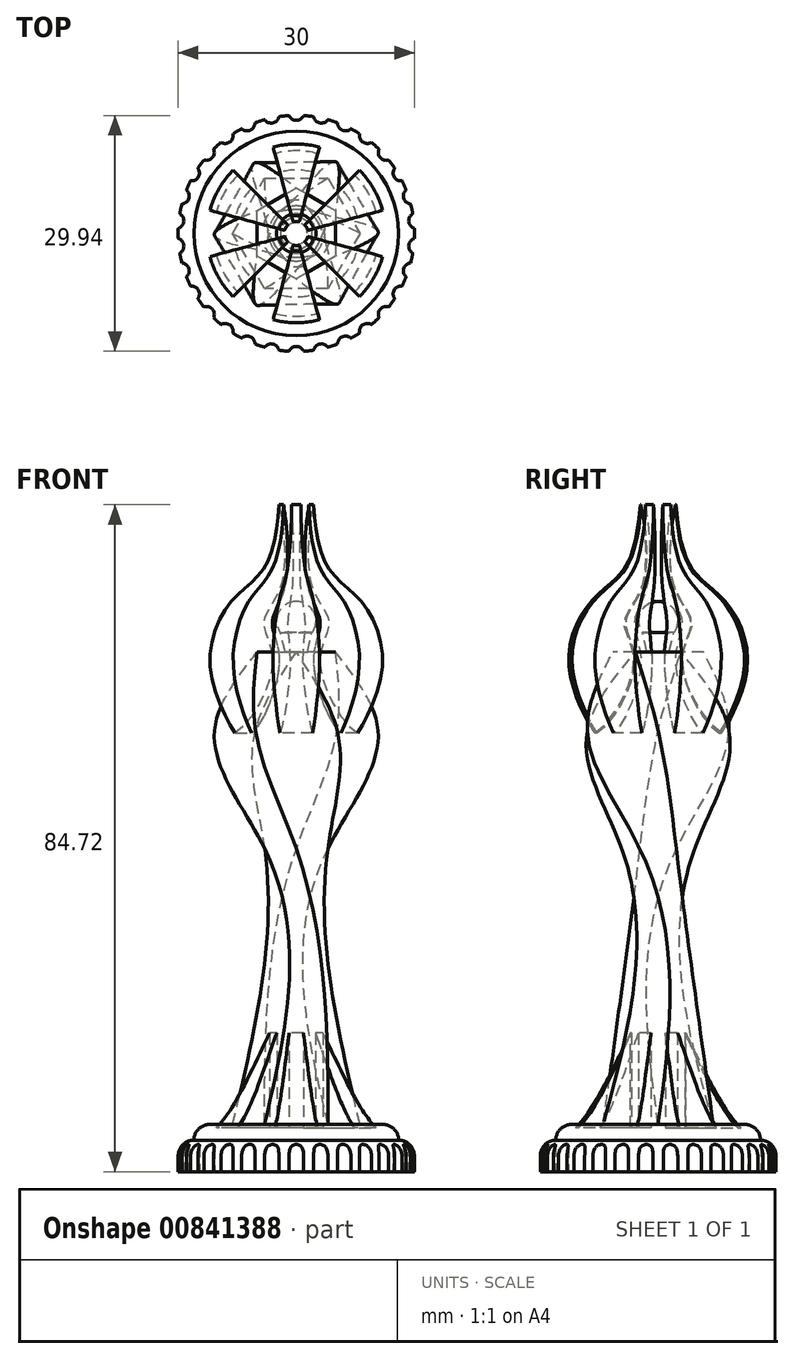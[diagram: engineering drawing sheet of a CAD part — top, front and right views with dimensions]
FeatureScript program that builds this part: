
annotation { "Feature Type Name" : "Feature", "Feature Type Description" : "" }
export const myFeature = defineFeature(function(context is Context, id is Id, definition is map)
    precondition{}
    {
        {
            var Q0;
            Q0=qCreatedBy(makeId("Top.planeOp"),FACE);
            var sketch = newSketch(context, id + "F0", { "sketchPlane" : qUnion([Q0])});
            skCircle(sketch, "E0", {"center": v(0, 0) * mm, "radius": 15 * mm});
            skSolve(sketch);
        }
        {
            var Q0;
            Q0=qSketchRegion(id+"F0",true);
            extrude(context, id + "F1", {"entities" : qUnion([Q0]), "depth" : 4 * mm, "offsetDistance" : 25 * mm});
        }
        {
            var Q0;
            Q0=makeQuery(id+"F1.opExtrude","CAP_FACE",FACE,{"disambiguationData":[OSD([sQuery(id+"F0.wireOp",EDGE,"E0")])],"isStart":false});
            var sketch = newSketch(context, id + "F2", { "sketchPlane" : qUnion([Q0])});
            skCircle(sketch, "E1", {"center": v(0, 0) * mm, "radius": 13 * mm});
            skSolve(sketch);
        }
        {
            var Q0;
            Q0=qSketchRegion(id+"F2",true);
            extrude(context, id + "F3", {"entities" : qUnion([Q0]), "operationType" : NewBodyOperationType.ADD, "depth" : 2 * mm, "offsetDistance" : 25 * mm});
        }
        {
            var Q0;
            Q0=makeQuery(id+"F1.opExtrude","CAP_EDGE",EDGE,{"disambiguationData":[OSD([sQuery(id+"F0.wireOp",EDGE,"E0")])],"isStart":false});
            var Q1;
            Q1=makeQuery(id+"F3.opExtrude","CAP_EDGE",EDGE,{"disambiguationData":[OSD([sQuery(id+"F2.wireOp",EDGE,"E1")])],"isStart":false});
            fillet(context, id + "F4", {"entities" : qUnion([Q0, Q1]), "radius" : 2 * mm, "tangentPropagation" : true, "allowEdgeOverflow" : false});
        }
        {
            var Q0;
            Q0=makeQuery(id+"F1.opExtrude","CAP_FACE",FACE,{"disambiguationData":[OSD([sQuery(id+"F0.wireOp",EDGE,"E0")])],"isStart":true});
            var sketch = newSketch(context, id + "F5", { "sketchPlane" : qUnion([Q0])});
            skCircle(sketch, "E2", {"center": v(0, 15.36) * mm, "radius": 1 * mm});
            skCircle(sketch, "E3.1.0", {"center": v(-3.2, 15.02) * mm, "radius": 1 * mm});
            skCircle(sketch, "E3.2.0", {"center": v(-6.25, 14.03) * mm, "radius": 1 * mm});
            skCircle(sketch, "E3.3.0", {"center": v(-9.03, 12.43) * mm, "radius": 1 * mm});
            skCircle(sketch, "E3.4.0", {"center": v(-11.41, 10.28) * mm, "radius": 1 * mm});
            skCircle(sketch, "E3.5.0", {"center": v(-13.3, 7.68) * mm, "radius": 1 * mm});
            skCircle(sketch, "E3.6.0", {"center": v(-14.6, 4.75) * mm, "radius": 1 * mm});
            skCircle(sketch, "E3.7.0", {"center": v(-15.27, 1.6) * mm, "radius": 1 * mm});
            skCircle(sketch, "E3.8.0", {"center": v(-15.27, -1.6) * mm, "radius": 1 * mm});
            skCircle(sketch, "E3.9.0", {"center": v(-14.6, -4.75) * mm, "radius": 1 * mm});
            skCircle(sketch, "E3.10.0", {"center": v(-13.3, -7.68) * mm, "radius": 1 * mm});
            skCircle(sketch, "E3.11.0", {"center": v(-11.41, -10.28) * mm, "radius": 1 * mm});
            skCircle(sketch, "E3.12.0", {"center": v(-9.03, -12.43) * mm, "radius": 1 * mm});
            skCircle(sketch, "E3.13.0", {"center": v(-6.25, -14.03) * mm, "radius": 1 * mm});
            skCircle(sketch, "E3.14.0", {"center": v(-3.2, -15.02) * mm, "radius": 1 * mm});
            skCircle(sketch, "E3.15.0", {"center": v(0, -15.36) * mm, "radius": 1 * mm});
            skCircle(sketch, "E3.16.0", {"center": v(3.2, -15.02) * mm, "radius": 1 * mm});
            skCircle(sketch, "E3.17.0", {"center": v(6.25, -14.03) * mm, "radius": 1 * mm});
            skCircle(sketch, "E3.18.0", {"center": v(9.03, -12.43) * mm, "radius": 1 * mm});
            skCircle(sketch, "E3.19.0", {"center": v(11.41, -10.28) * mm, "radius": 1 * mm});
            skCircle(sketch, "E3.20.0", {"center": v(13.3, -7.68) * mm, "radius": 1 * mm});
            skCircle(sketch, "E3.21.0", {"center": v(14.6, -4.75) * mm, "radius": 1 * mm});
            skCircle(sketch, "E3.22.0", {"center": v(15.27, -1.6) * mm, "radius": 1 * mm});
            skCircle(sketch, "E3.23.0", {"center": v(15.27, 1.6) * mm, "radius": 1 * mm});
            skCircle(sketch, "E3.24.0", {"center": v(14.6, 4.75) * mm, "radius": 1 * mm});
            skCircle(sketch, "E3.25.0", {"center": v(13.3, 7.68) * mm, "radius": 1 * mm});
            skCircle(sketch, "E3.26.0", {"center": v(11.41, 10.28) * mm, "radius": 1 * mm});
            skCircle(sketch, "E3.27.0", {"center": v(9.03, 12.43) * mm, "radius": 1 * mm});
            skCircle(sketch, "E3.28.0", {"center": v(6.25, 14.03) * mm, "radius": 1 * mm});
            skCircle(sketch, "E3.29.0", {"center": v(3.2, 15.02) * mm, "radius": 1 * mm});
            skPoint(sketch, "E3.center", {"position": v(0, 0) * mm});
            skSolve(sketch);
        }
        {
            var Q0;
            Q0=qSketchRegion(id+"F5",true);
            extrude(context, id + "F6", {"entities" : qUnion([Q0]), "operationType" : NewBodyOperationType.REMOVE, "oppositeDirection" : true, "depth" : 25 * mm, "offsetDistance" : 25 * mm});
        }
        {
            var Q0;
            Q0=makeQuery(id+"F3.opExtrude","CAP_FACE",FACE,{"disambiguationData":[OSD([sQuery(id+"F2.wireOp",EDGE,"E1")])],"isStart":false});
            var sketch = newSketch(context, id + "F7", { "sketchPlane" : qUnion([Q0])});
            skCircle(sketch, "E4.cCircle", {"center": v(0, 0) * mm, "radius": 7 * mm, "construction": true});
            skLineSegment(sketch, "E4.0", {"start": v(8.08, 0) * mm, "end": v(4.04, -7) * mm});
            skLineSegment(sketch, "E4.1", {"start": v(4.04, -7) * mm, "end": v(-4.04, -7) * mm});
            skLineSegment(sketch, "E4.2", {"start": v(-4.04, -7) * mm, "end": v(-8.08, 0) * mm});
            skLineSegment(sketch, "E4.3", {"start": v(-8.08, 0) * mm, "end": v(-4.04, 7) * mm});
            skLineSegment(sketch, "E4.4", {"start": v(-4.04, 7) * mm, "end": v(4.04, 7) * mm});
            skLineSegment(sketch, "E4.5", {"start": v(4.04, 7) * mm, "end": v(8.08, 0) * mm});
            skPoint(sketch, "E4.0.midPoint", {"position": v(6.06, -3.5) * mm});
            skSolve(sketch);
        }
        {
            var Q0;
            Q0=makeQuery(id+"F3.opExtrude","CAP_FACE",FACE,{"disambiguationData":[OSD([sQuery(id+"F2.wireOp",EDGE,"E1")])],"isStart":false});
            cPlane(context, id + "F8", {"entities" : qUnion([Q0]), "cplaneType" : CPlaneType.OFFSET, "offset" : 35 * mm, "width" : 150 * mm, "height" : 150 * mm});
        }
        {
            var Q0;
            Q0=qCreatedBy(id+"F8.planeOp",FACE);
            var sketch = newSketch(context, id + "F9", { "sketchPlane" : qUnion([Q0])});
            skCircle(sketch, "E5.cCircle", {"center": v(0, 0) * mm, "radius": 4 * mm, "construction": true});
            skLineSegment(sketch, "E5.0", {"start": v(4, 2.3) * mm, "end": v(4, -2.3) * mm});
            skLineSegment(sketch, "E5.1", {"start": v(4, -2.3) * mm, "end": v(0, -4.62) * mm});
            skLineSegment(sketch, "E5.2", {"start": v(0, -4.62) * mm, "end": v(-4, -2.3) * mm});
            skLineSegment(sketch, "E5.3", {"start": v(-4, -2.3) * mm, "end": v(-4, 2.3) * mm});
            skLineSegment(sketch, "E5.4", {"start": v(-4, 2.3) * mm, "end": v(0, 4.62) * mm});
            skLineSegment(sketch, "E5.5", {"start": v(0, 4.62) * mm, "end": v(4, 2.3) * mm});
            skPoint(sketch, "E5.0.midPoint", {"position": v(4, 0) * mm});
            skSolve(sketch);
        }
        {
            var Q0;
            Q0=qCreatedBy(id+"F8.planeOp",FACE);
            cPlane(context, id + "F10", {"entities" : qUnion([Q0]), "cplaneType" : CPlaneType.OFFSET, "offset" : 15 * mm, "width" : 150 * mm, "height" : 150 * mm});
        }
        {
            var Q0;
            Q0=qCreatedBy(id+"F10.planeOp",FACE);
            var sketch = newSketch(context, id + "F11", { "sketchPlane" : qUnion([Q0])});
            skCircle(sketch, "E6.cCircle", {"center": v(0, 0) * mm, "radius": 9 * mm, "construction": true});
            skLineSegment(sketch, "E6.0", {"start": v(5.2, -9) * mm, "end": v(-5.2, -9) * mm});
            skLineSegment(sketch, "E6.1", {"start": v(-5.2, -9) * mm, "end": v(-10.4, 0) * mm});
            skLineSegment(sketch, "E6.2", {"start": v(-10.4, 0) * mm, "end": v(-5.2, 9) * mm});
            skLineSegment(sketch, "E6.3", {"start": v(-5.2, 9) * mm, "end": v(5.2, 9) * mm});
            skLineSegment(sketch, "E6.4", {"start": v(5.2, 9) * mm, "end": v(10.4, 0) * mm});
            skLineSegment(sketch, "E6.5", {"start": v(10.4, 0) * mm, "end": v(5.2, -9) * mm});
            skPoint(sketch, "E6.0.midPoint", {"position": v(0, -9) * mm});
            skSolve(sketch);
        }
        {
            var Q0;
            Q0=qCreatedBy(id+"F10.planeOp",FACE);
            cPlane(context, id + "F12", {"entities" : qUnion([Q0]), "cplaneType" : CPlaneType.OFFSET, "offset" : 10 * mm, "width" : 150 * mm, "height" : 150 * mm});
        }
        {
            var Q0;
            Q0=qCreatedBy(id+"F12.planeOp",FACE);
            var sketch = newSketch(context, id + "F13", { "sketchPlane" : qUnion([Q0])});
            skCircle(sketch, "E7.cCircle", {"center": v(0, 0) * mm, "radius": 5 * mm, "construction": true});
            skLineSegment(sketch, "E7.0", {"start": v(5, 2.89) * mm, "end": v(5, -2.89) * mm});
            skLineSegment(sketch, "E7.1", {"start": v(5, -2.89) * mm, "end": v(0, -5.77) * mm});
            skLineSegment(sketch, "E7.2", {"start": v(0, -5.77) * mm, "end": v(-5, -2.89) * mm});
            skLineSegment(sketch, "E7.3", {"start": v(-5, -2.89) * mm, "end": v(-5, 2.89) * mm});
            skLineSegment(sketch, "E7.4", {"start": v(-5, 2.89) * mm, "end": v(0, 5.77) * mm});
            skLineSegment(sketch, "E7.5", {"start": v(0, 5.77) * mm, "end": v(5, 2.89) * mm});
            skPoint(sketch, "E7.0.midPoint", {"position": v(5, 0) * mm});
            skSolve(sketch);
        }
        {
            var Q1;
            Q1=makeQuery(id+"F7.imprint","IMPRINT",FACE,{"disambiguationData":[TD([[makeQuery(id+"F7.imprint","IMPRINT",EDGE,{"derivedFrom":sQuery(id+"F7.wireOp",EDGE,"E4.0")}),-1.0]])]});
            var Q2;
            Q2=makeQuery(id+"F9.imprint","IMPRINT",FACE,{"disambiguationData":[TD([[makeQuery(id+"F9.imprint","IMPRINT",EDGE,{"derivedFrom":sQuery(id+"F9.wireOp",EDGE,"E5.0")}),-1.0]])]});
            var Q3;
            Q3=makeQuery(id+"F11.imprint","IMPRINT",FACE,{"disambiguationData":[TD([[makeQuery(id+"F11.imprint","IMPRINT",EDGE,{"derivedFrom":sQuery(id+"F11.wireOp",EDGE,"E6.0")}),-1.0]])]});
            var Q4;
            Q4=makeQuery(id+"F13.imprint","IMPRINT",FACE,{"disambiguationData":[TD([[makeQuery(id+"F13.imprint","IMPRINT",EDGE,{"derivedFrom":sQuery(id+"F13.wireOp",EDGE,"E7.0")}),-1.0]])]});
            var Q5;
            Q5=sQuery(id+"F7.wireOp",VERTEX,"E4.2.end");
            var Q6;
            Q6=sQuery(id+"F9.wireOp",VERTEX,"E5.3.end");
            var Q7;
            Q7=sQuery(id+"F11.wireOp",VERTEX,"E6.2.end");
            var Q8;
            Q8=sQuery(id+"F13.wireOp",VERTEX,"E7.4.end");
            loft(context, id + "F14", {"operationType" : NewBodyOperationType.ADD, "sheetProfilesArray" : [{ "sheetProfileEntities" : qUnion([Q1]) }, { "sheetProfileEntities" : qUnion([Q2]) }, { "sheetProfileEntities" : qUnion([Q3]) }, { "sheetProfileEntities" : qUnion([Q4]) }], "matchConnections" : true, "connections" : [{ "connectionEntities" : qUnion([Q5, Q6, Q7, Q8]), "connectionEdgeQueries" : qUnion([]), "connectionEdgeParameters" : [] }]});
        }
        {
            var Q0;
            Q0=qCreatedBy(makeId("Right.planeOp"),FACE);
            var sketch = newSketch(context, id + "F15", { "sketchPlane" : qUnion([Q0])});
            skFitSpline(sketch, "E8", {"points": [v(-8.05, 55.74) * mm, v(-11.34, 64.65) * mm, v(-8.34, 72.64) * mm, v(-4.25, 76.65) * mm, v(-2.28, 84.72) * mm], "startDerivative": vector(-13.8, 20.44) * mm, "endDerivative": vector(2.17, 36.52) * mm});
            skFitSpline(sketch, "E9", {"points": [v(-2.28, 84.72) * mm, v(-1.63, 80.56) * mm, v(-2.28, 73.75) * mm, v(-4.3, 69.72) * mm, v(-3.08, 64.73) * mm, v(-8.05, 55.74) * mm], "startDerivative": vector(4.7, -22.47) * mm, "endDerivative": vector(-23.16, -12.62) * mm});
            skLineSegment(sketch, "E10", {"start": v(0, 38.47) * mm, "end": v(0, 65.66) * mm, "construction": true});
            skSolve(sketch);
        }
        {
            var Q0;
            Q0 = qSketchRegion(id + "F15", true);
            var Q1;
            Q1=sQuery(id+"F15.wireOp",EDGE,"E10");
            revolve(context, id + "F16", {"surfaceOperationType" : NewSurfaceOperationType.NEW, "entities" : qUnion([Q0]), "axis" : qUnion([Q1]), "revolveType" : RevolveType.SYMMETRIC, "angle" : 30 * degree});
        }
        {
            var Q0;
            Q0=makeQuery(id+"F16.opRevolve","SWEPT_BODY",BODY,{"disambiguationData":[OSD([sQuery(id+"F15.wireOp",EDGE,"E8"),sQuery(id+"F15.wireOp",EDGE,"E9")])]});
            var Q1;
            Q1=sQuery(id+"F15.wireOp",EDGE,"E10");
            circularPattern(context, id + "F17", {"entities" : qUnion([Q0]), "axis" : qUnion([Q1]), "angle" : 360 * degree, "instanceCount" : 6, "equalSpace" : true});
        }
        {
            var Q0;
            Q0=qCreatedBy(makeId("Right.planeOp"),FACE);
            var sketch = newSketch(context, id + "F18", { "sketchPlane" : qUnion([Q0])});
            skArc(sketch, "E11", {"start": v(0, 72.45) * mm, "mid": v(-2.23, 71.08) * mm, "end": v(-2.01, 68.47) * mm});
            skLineSegment(sketch, "E12", {"start": v(-2.01, 68.47) * mm, "end": v(-1.4, 66) * mm});
            skLineSegment(sketch, "E13", {"start": v(-1.4, 66) * mm, "end": v(0, 66) * mm});
            skLineSegment(sketch, "E14", {"start": v(0, 73) * mm, "end": v(0, 65.68) * mm});
            skPoint(sketch, "E15.end.orphan", {"position": v(2.01, 68.47) * mm});
            skSolve(sketch);
        }
        {
            var Q0;
            Q0 = qSketchRegion(id + "F18", true);
            var Q1;
            Q1=sQuery(id+"F15.wireOp",EDGE,"E10");
            revolve(context, id + "F19", {"operationType" : NewBodyOperationType.ADD, "surfaceOperationType" : NewSurfaceOperationType.NEW, "entities" : qUnion([Q0]), "axis" : qUnion([Q1]), "revolveType" : RevolveType.FULL});
        }
        {
            var Q0;
            {var subQ0=sQuery(id+"F2.wireOp",EDGE,"E1");Q0=makeQuery(id+"F4.opFillet","BLEND_EDGE",EDGE,{"blendedFrom":[makeQuery(id+"F3.opExtrude","CAP_EDGE",EDGE,{"disambiguationData":[OSD([subQ0])],"isStart":false}),makeQuery(id+"F3.opExtrude","CAP_FACE",FACE,{"disambiguationData":[OSD([subQ0])],"isStart":false})],"blendedInto":[makeQuery(id+"F3.opExtrude","CAP_FACE",FACE,{"disambiguationData":[OSD([subQ0])],"isStart":false})]});}
            cPlane(context, id + "F20", {"entities" : qUnion([Q0]), "cplaneType" : CPlaneType.LINE_ANGLE, "offset" : 25 * mm, "angle" : 60 * degree, "width" : 150 * mm, "height" : 150 * mm});
        }
        {
            var Q0;
            Q0=qCreatedBy(id+"F20.planeOp",FACE);
            var sketch = newSketch(context, id + "F21", { "sketchPlane" : qUnion([Q0])});
            skFitSpline(sketch, "E16", {"points": [v(-10.5, 5.56) * mm, v(-7.5, 9.76) * mm, v(-3.5, 17.64) * mm], "startDerivative": vector(6.4, 6.37) * mm, "endDerivative": vector(2.44, 4.6) * mm});
            skLineSegment(sketch, "E17", {"start": v(-3.5, 17.64) * mm, "end": v(-3.5, 5.56) * mm});
            skLineSegment(sketch, "E18", {"start": v(-3.5, 5.56) * mm, "end": v(-10.5, 5.56) * mm});
            skSolve(sketch);
        }
        {
            var Q0;
            Q0 = qSketchRegion(id + "F21", true);
            var Q1;
            Q1=sQuery(id+"F15.wireOp",EDGE,"E10");
            revolve(context, id + "F22", {"surfaceOperationType" : NewSurfaceOperationType.NEW, "entities" : qUnion([Q0]), "axis" : qUnion([Q1]), "revolveType" : RevolveType.SYMMETRIC, "oppositeDirection" : true, "angle" : 30 * degree});
        }
        {
            var Q0;
            Q0=makeQuery(id+"F22.opRevolve","SWEPT_BODY",BODY,{"disambiguationData":[OSD([sQuery(id+"F21.wireOp",EDGE,"E16"),sQuery(id+"F21.wireOp",EDGE,"E17"),sQuery(id+"F21.wireOp",EDGE,"E18")])]});
            var Q1;
            Q1=sQuery(id+"F15.wireOp",EDGE,"E10");
            circularPattern(context, id + "F23", {"entities" : qUnion([Q0]), "axis" : qUnion([Q1]), "angle" : 360 * degree, "instanceCount" : 6, "equalSpace" : true});
        }
    });
